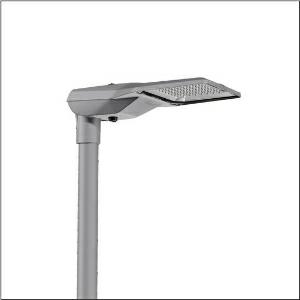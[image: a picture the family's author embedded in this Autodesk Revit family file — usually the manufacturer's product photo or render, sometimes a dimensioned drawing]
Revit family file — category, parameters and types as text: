
# Revit family: streetlight_sl_21_iq_midi___st1_0ab_5xe3m31y08nb_fb51
name_source: partatom
category: Lighting Fixtures
units: mm (PartAtom-declared; Revit-internal decimal feet)

## family parameters
Cut with Voids When Loaded = No
Host = Face
Light Source = No
Part Type = Normal
Room Calculation Point = No
Round Connector Dimension = Use Diameter
Shared = No

## types (1)
- --- (1 x LED, 18970 lm, 136.6 W, 3000K)
    Apparent Load = 137 VA
    CIE Flux Codes = 40 74 97 100 100
    Color Rendering = 70
    Color Temperature = 3000K
    Default Elevation = 1800 mm
    Description = Streetlight SL 21 iQ midi, mast luminaire, primary light control with lens, of PMMA, primary optical cover: cover, of toughened safety glass, transparent, light distribution: ST1.0aB, light emission: direct distribution, primary light characteristic: asymmetric, installation type: post-top, side-entry, LED, High Power LED, rated luminous flux: 18.970lm, luminous efficacy: 139lm/W, light colour: 730, colour temperature: 3000K, control gear: iQ-Street Remote, D4i with power reduction, control: pre-setting: logarithmic dimming characteristic, Street-Remote, Auto-Match, Temp-Guard, Lumen-Switch, Night-Set, Smart-Wire, Light-Fading, Desk-Remote (wireless, voltage-free reading and setting of iQ features in the workshop via application-optimized NFC function/RFID function), optimised constant luminous flux control (CLO 2.0), mains connection: 230..240V, AC, 50/60Hz, start of lifetime: 137W, end of service life: 144W, reduction: 61W, luminaire housing, of diecast aluminium, powder-coated, Siteco® metallic grey (DB 702S), corrosivity category C5 mid according to DIN EN ISO 12944, please order mast flange separately, inclination adjustable: 0°, 5°, 10°, 15°, sealing non-destructively replaceable, multi-level sealing system, length: 644mm, width: 335mm, height: 110mm, mast flange for spigot size: 42mm (side-entry): 5XC10008XM4, 60/48mm (side-entry/post-top): 5XC10108XM2, 76/60mm (side-entry/post-top): 5XC10108XM1, mounting height: 4..8m, Smart Interface below and above, protection rating (complete): IP66, insulation class (complete): insulation class II (safety insulation), certification: CE, ENEC, ENEC+, VDE, impact resistance: IK10, permissible operating ambient temperature for outdoor applications: -40..+50°C, standard-compliant lighting for roads and squares, packaging unit: 1 piece

Light Distribution: ST1.0aB
    Height = 111 mm
    Lamp = 1 x LED
    Lamp Light Flux = 18970 lm
    Lamp Power = 136.6 W
    Lamp count = 1
    Length = 644 mm
    Luminous efficacy = 139 lm/W
    Manufacturer = Siteco
    ModVariant = No
    Model = 5XE3M31Y08NB
    Number of Poles = 1
    OnlyDefault = Yes
    Power Factor = 1
    Product Name = Streetlight SL 21 iQ midi | ST1.0aB
    Product group = mast luminaire | pylon top
    ProductGroupID = 6100
    Protection Class = Protection class II
    Protection Degree = IP 66
    RLX_Detail_Level = 1
    RLX_Emergency_Light_Flux = 0 lm
    RLX_Emergency_Type = 0
    RLX_Emergency_Type_DB = No
    RlxData = <blob elided: 91353 chars, md5=c7bee595>
    Socket = socket
    Standby Power = 0 W
    System Light Flux = 18970 lm
    System Power = 137 W
    Type Comments = factory setting: luminous flux: 100 % | dim-lin: 254 | 733 mA
    Type Image = l_1004304.jpg
    URL = http://relux.com
    VarID = @adj_133535
    Voltage = 0 V
    Weight = 0.00 kg
    Width = 336 mm

## geometry (parser evidence)
native form markers: Blend x4, Sweep x10
no freeform markers — native parametric forms only
